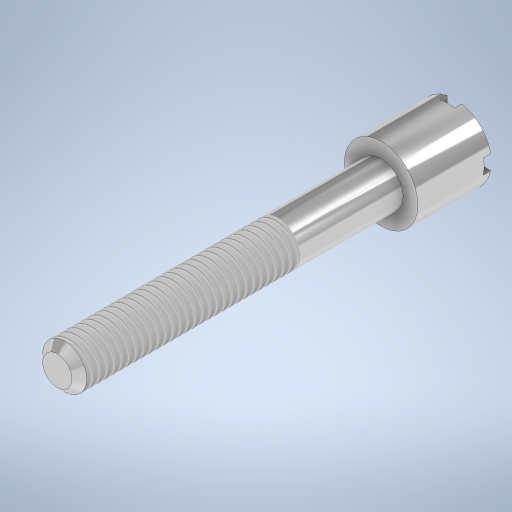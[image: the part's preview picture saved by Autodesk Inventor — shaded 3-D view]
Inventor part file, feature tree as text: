
AUTODESK INVENTOR PART (.ipt)
format: ipt  version: 2023 (Build 270158000, 158)  size: 332,288 bytes
history: native  units: mm
features: sketch x4, extrude x3, chamfer x2, other x1, thread x1, hole x1
ambient origin geometry x8: Origin, YZ Plane, XZ Plane, XY Plane, X Axis, Y Axis, Z Axis, Center Point
bodies: Body1 (feature_tree)
feature tree (12):
  other  "Sólido1"
  extrude  "Extrusão1"  Depth=5.0mm TaperAngle=0.0deg
  extrude  "Extrusão2"  Depth=22.0mm TaperAngle=0.0deg
  thread  "Rosca1"  [1 undecoded]
  hole  "Furo1"  [1 undecoded]
  extrude  "Extrusão3"  Depth=1.0mm
  chamfer  "Chanfro1"  Distance=6.0mm
  chamfer  "Chanfro2"  Distance=6.0mm
  sketch  "Esboço1"  dims[d0=5.0mm d1=5.0mm d2=0.0mm]
  sketch  "Esboço2"  dims[d3=3.0mm d4=22.0mm d5=0.0mm d6=15.0mm d7=7.0mm]
  sketch  "Esboço3"  dims[d8=2.459mm d9=4.0mm d10=4.0mm d11=2.0mm d12=90.0deg d13=4.0mm d14=20.594885mm d15=0.0mm]
  sketch  "Esboço4"  dims[d16=0.0mm d17=1.0mm d18=6.0mm d19=6.0mm d20=1.0mm d21=0.5mm d22=0.0mm d23=1.27mm d24=2.0mm d25=45.0deg d26=0.5mm d27=2.0mm d28=45.0deg]
note: 2 required parameter values undecoded (feature->parameter linkage not recoverable at this tier; creation-order binding heuristic only, values carry confidence <= 0.55)
